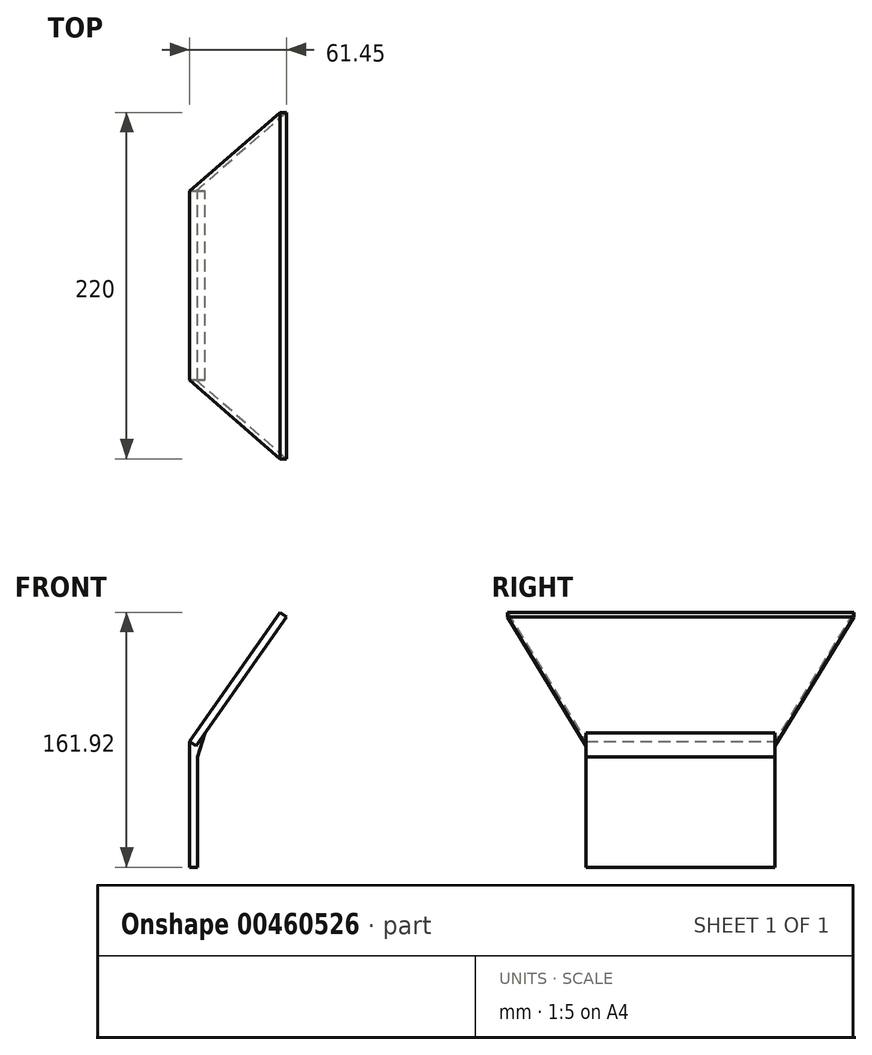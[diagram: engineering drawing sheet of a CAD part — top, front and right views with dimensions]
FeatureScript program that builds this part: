
annotation { "Feature Type Name" : "Feature", "Feature Type Description" : "" }
export const myFeature = defineFeature(function(context is Context, id is Id, definition is map)
    precondition{}
    {
        {
            var Q0;
            Q0=qCreatedBy(makeId("Front.planeOp"),FACE);
            var sketch = newSketch(context, id + "F0", { "sketchPlane" : qUnion([Q0])});
            skLineSegment(sketch, "E0", {"start": v(0, 0) * mm, "end": v(0, 80) * mm});
            skLineSegment(sketch, "E1", {"start": v(0, 80) * mm, "end": v(57.36, 161.92) * mm});
            skLineSegment(sketch, "E2", {"start": v(0, 0) * mm, "end": v(5, 0) * mm});
            skLineSegment(sketch, "E3", {"start": v(5, 0) * mm, "end": v(5, 70) * mm});
            skLineSegment(sketch, "E4", {"start": v(9.83, 85.32) * mm, "end": v(61.45, 159.05) * mm});
            skLineSegment(sketch, "E5", {"start": v(61.45, 159.05) * mm, "end": v(57.36, 161.92) * mm});
            skLineSegment(sketch, "E6", {"start": v(9.83, 85.32) * mm, "end": v(5, 70) * mm});
            skSolve(sketch);
        }
        {
            var Q0;
            Q0=makeQuery(id+"F0.imprint","IMPRINT",FACE,{"disambiguationData":[TD([[makeQuery(id+"F0.imprint","IMPRINT",EDGE,{"derivedFrom":sQuery(id+"F0.wireOp",EDGE,"E0")}),-1.0]])]});
            extrude(context, id + "F1", {"entities" : qUnion([Q0]), "depth" : 120 * mm});
        }
        {
            var Q0;
            Q0=makeQuery(id+"F1.opExtrude","SWEPT_FACE",FACE,{"disambiguationData":[OSD([sQuery(id+"F0.wireOp",EDGE,"E1")])]});
            var sketch = newSketch(context, id + "F2", { "sketchPlane" : qUnion([Q0])});
            skLineSegment(sketch, "E7", {"start": v(0, 165.53) * mm, "end": v(-50, 165.53) * mm});
            skLineSegment(sketch, "E8", {"start": v(-50, 165.53) * mm, "end": v(0, 65.53) * mm});
            skLineSegment(sketch, "E9", {"start": v(120, 165.53) * mm, "end": v(170, 165.53) * mm});
            skLineSegment(sketch, "E10", {"start": v(170, 165.53) * mm, "end": v(120, 65.53) * mm});
            skSolve(sketch);
        }
        {
            var Q0;
            Q0=makeQuery(id+"F2.imprint","IMPRINT",FACE,{"disambiguationData":[TD([[makeQuery(id+"F2.imprint","IMPRINT",EDGE,{"derivedFrom":sQuery(id+"F2.wireOp",EDGE,"E7")}),1.0]])]});
            extrude(context, id + "F3", {"entities" : qUnion([Q0]), "operationType" : NewBodyOperationType.ADD, "oppositeDirection" : true, "depth" : 5 * mm});
        }
        {
            var Q0;
            Q0=makeQuery(id+"F2.imprint","IMPRINT",FACE,{"disambiguationData":[TD([[makeQuery(id+"F2.imprint","IMPRINT",EDGE,{"derivedFrom":sQuery(id+"F2.wireOp",EDGE,"E9")}),-1.0]])]});
            extrude(context, id + "F4", {"entities" : qUnion([Q0]), "operationType" : NewBodyOperationType.ADD, "oppositeDirection" : true, "depth" : 5 * mm});
        }
    });
